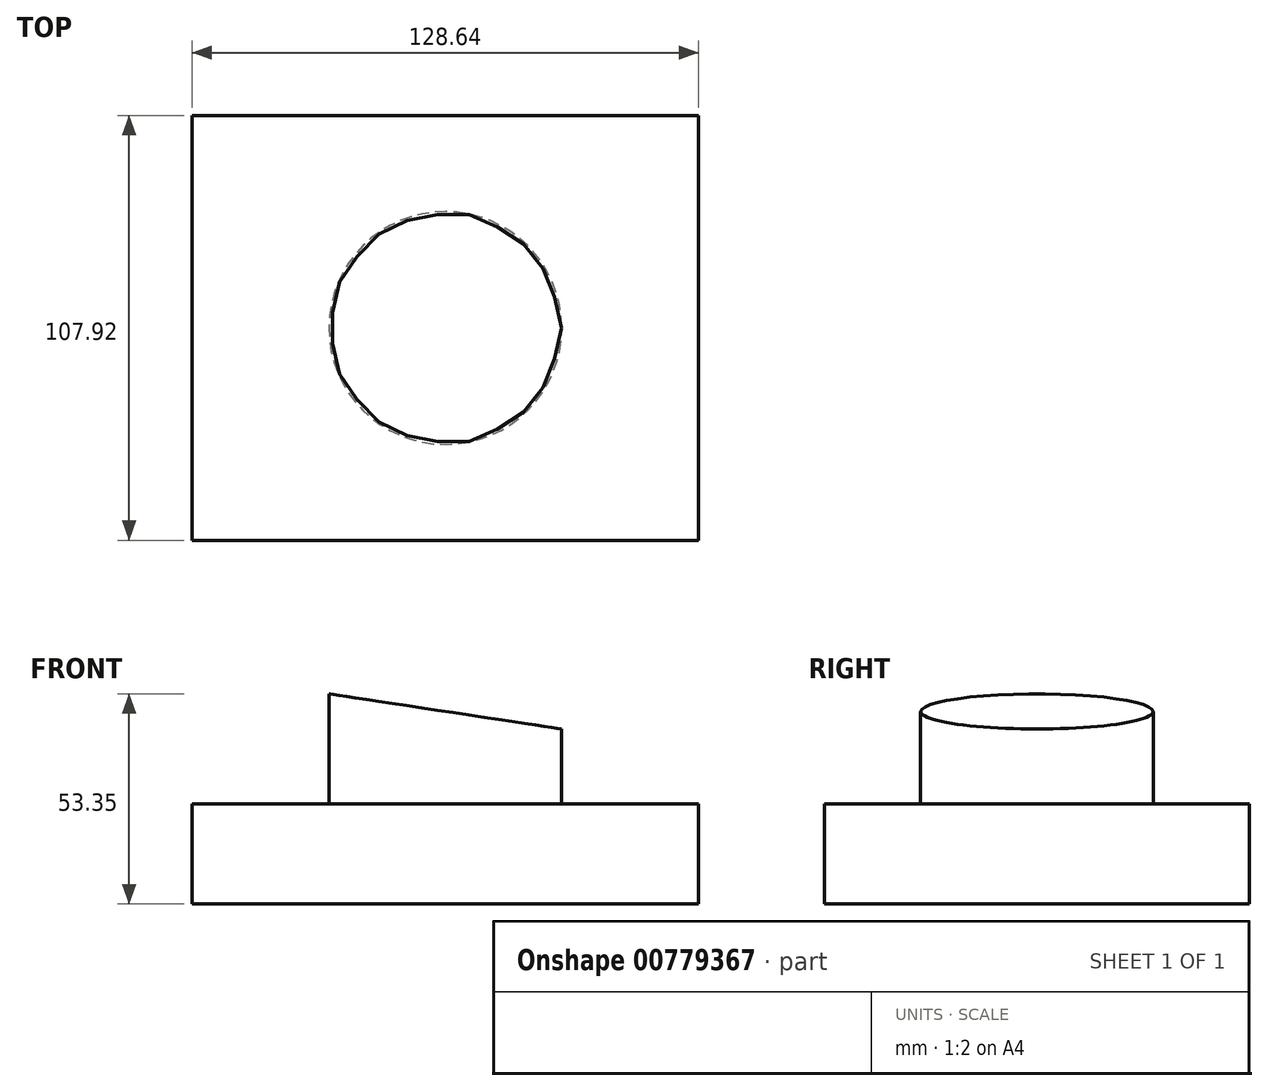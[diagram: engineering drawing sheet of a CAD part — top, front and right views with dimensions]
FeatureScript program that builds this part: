
annotation { "Feature Type Name" : "Feature", "Feature Type Description" : "" }
export const myFeature = defineFeature(function(context is Context, id is Id, definition is map)
    precondition{}
    {
        {
            var Q0;
            Q0=qCreatedBy(makeId("Top.planeOp"),FACE);
            var sketch = newSketch(context, id + "F0", { "sketchPlane" : qUnion([Q0])});
            skLineSegment(sketch, "E0.bottom", {"start": v(64.32, 53.96) * mm, "end": v(-64.32, 53.96) * mm});
            skLineSegment(sketch, "E0.top", {"start": v(64.32, -53.96) * mm, "end": v(-64.32, -53.96) * mm});
            skLineSegment(sketch, "E0.left", {"start": v(64.32, 53.96) * mm, "end": v(64.32, -53.96) * mm});
            skLineSegment(sketch, "E0.right", {"start": v(-64.32, 53.96) * mm, "end": v(-64.32, -53.96) * mm});
            skPoint(sketch, "E0.middle", {"position": v(0, 0) * mm});
            skSolve(sketch);
        }
        {
            var Q0;
            Q0 = qSketchRegion(id + "F0", true);
            extrude(context, id + "F1", {"entities" : qUnion([Q0]), "depth" : 25.4 * mm, "offsetDistance" : 25.4 * mm});
        }
        {
            var Q0;
            Q0=makeQuery(id+"F1.opExtrude","CAP_FACE",FACE,{"disambiguationData":[OSD([sQuery(id+"F0.wireOp",EDGE,"E0.bottom"),sQuery(id+"F0.wireOp",EDGE,"E0.top"),sQuery(id+"F0.wireOp",EDGE,"E0.left"),sQuery(id+"F0.wireOp",EDGE,"E0.right")])],"isStart":false});
            var sketch = newSketch(context, id + "F2", { "sketchPlane" : qUnion([Q0])});
            skCircle(sketch, "E1", {"center": v(0, 0) * mm, "radius": 29.58 * mm});
            skSolve(sketch);
        }
        {
            var Q0;
            Q0=makeQuery(id+"F2.imprint","IMPRINT",FACE,{"disambiguationData":[TD([[makeQuery(id+"F2.imprint","IMPRINT",EDGE,{"derivedFrom":sQuery(id+"F2.wireOp",EDGE,"E1")}),1.0]])]});
            var sketch = newSketch(context, id + "F3", { "sketchPlane" : qUnion([Q0])});
            skSolve(sketch);
        }
        {
            var Q0;
            Q0=makeQuery(id+"F3.imprint","IMPRINT",FACE,{"disambiguationData":[TD([[makeQuery(id+"F3.imprint","IMPRINT",EDGE,{"derivedFrom":makeQuery(id+"F2.imprint","IMPRINT",EDGE,{"derivedFrom":sQuery(id+"F2.wireOp",EDGE,"E1")})}),1.0]])]});
            extrude(context, id + "F4", {"entities" : qUnion([Q0]), "operationType" : NewBodyOperationType.ADD, "depth" : 36.32 * mm, "offsetDistance" : 25.4 * mm});
        }
        {
            var Q0;
            Q0=qCreatedBy(makeId("Front.planeOp"),FACE);
            var sketch = newSketch(context, id + "F5", { "sketchPlane" : qUnion([Q0])});
            skLineSegment(sketch, "E2", {"start": v(-46.15, 55.85) * mm, "end": v(49.92, 41.38) * mm});
            skLineSegment(sketch, "E3", {"start": v(49.92, 41.38) * mm, "end": v(30.24, 72.63) * mm});
            skLineSegment(sketch, "E4", {"start": v(30.24, 72.63) * mm, "end": v(-54.26, 60.48) * mm});
            skLineSegment(sketch, "E5", {"start": v(-54.26, 60.48) * mm, "end": v(-46.15, 55.85) * mm});
            skSolve(sketch);
        }
        {
            var Q0;
            Q0=makeQuery(id+"F5.imprint","IMPRINT",FACE,{"disambiguationData":[TD([[makeQuery(id+"F5.imprint","IMPRINT",EDGE,{"derivedFrom":sQuery(id+"F5.wireOp",EDGE,"E2")}),1.0]])]});
            extrude(context, id + "F6", {"entities" : qUnion([Q0]), "operationType" : NewBodyOperationType.REMOVE, "oppositeDirection" : true, "depth" : 38.1 * mm, "offsetDistance" : 25.4 * mm});
        }
        {
            var Q0;
            Q0=makeQuery(id+"F5.imprint","IMPRINT",FACE,{"disambiguationData":[TD([[makeQuery(id+"F5.imprint","IMPRINT",EDGE,{"derivedFrom":sQuery(id+"F5.wireOp",EDGE,"E2")}),1.0]])]});
            extrude(context, id + "F7", {"entities" : qUnion([Q0]), "operationType" : NewBodyOperationType.REMOVE, "depth" : 63 * mm, "offsetDistance" : 25.4 * mm});
        }
    });
